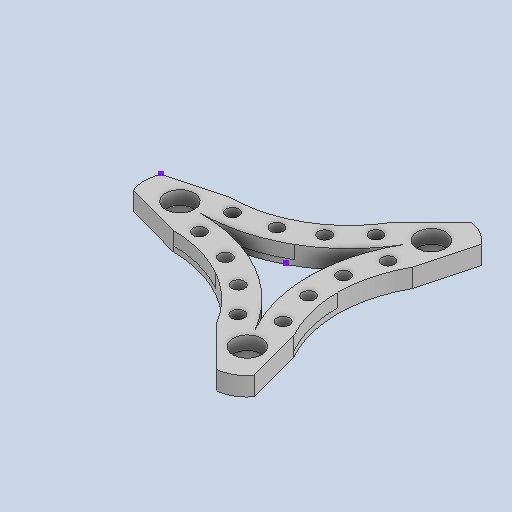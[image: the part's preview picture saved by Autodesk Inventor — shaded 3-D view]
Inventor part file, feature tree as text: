
AUTODESK INVENTOR PART (.ipt)
format: ipt  version: 2022.4 (Build 264492010, 492A)  size: 165,376 bytes
history: native  units: mm
features: other x1, sketch x1
ambient origin geometry x8: Origin, YZ Plane, XZ Plane, XY Plane, X Axis, Y Axis, Z Axis, Center Point
bodies: Solid2 (feature_tree), Solid1 (feature_tree)
feature tree (2):
  other  "Repaired Geometry1"
  sketch  "Sketch1"
